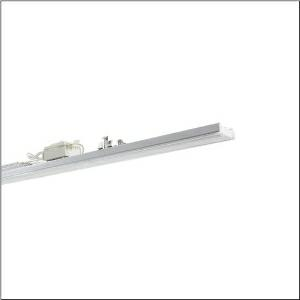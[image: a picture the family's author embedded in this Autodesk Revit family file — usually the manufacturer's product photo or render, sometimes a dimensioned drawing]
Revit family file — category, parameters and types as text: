
# Revit family: licross_r__21_recessed_mo_52tl12dn68xg3s_127a
name_source: partatom
category: Lighting Fixtures
units: mm (PartAtom-declared; Revit-internal decimal feet)

## family parameters
Cut with Voids When Loaded = No
Host = Face
Light Source = No
Part Type = Normal
Room Calculation Point = No
Round Connector Dimension = Use Diameter
Shared = No

## types (1)
- --- (1 x LED, 920 lm, 6.7 W, 6500K)
    Apparent Load = 7 VA
    CIE Flux Codes = 72 92 99 100 100
    Color Rendering = 80
    Color Temperature = 6500K
    Default Elevation = 1800 mm
    Description = Licross® 21 Recessed MO, luminaire insert, of sheet steel, galvanised, coil coated, white, length: 1.500mm, width: 66mm, height: 67mm, LED rated luminous flux: 8.000lm, light colour: 865, control gear: DALI 2 (for two DALI lines), with plug, 6-pole, with phase selection, for trunking rail, 14-core, mains connection: 220..240V, AC, 50/60Hz, rated input power: 46W, for emergency light function, halogen-free wiring, for trunking rail, 14-core, converter,control gear: single battery element, battery: LiFePO4, 9Ah, primary optical cover: cover, of PMMA, light emission: direct distribution, primary light characteristic: symmetric, protection rating (complete): IP40, insulation class (complete): insulation class I (protective earthing), certification: CE, UKCA, protection symbol: D if used in an environment without relevant dust loads with corresponding accessories, impact resistance: IK06, permissible ambient temperature for indoor applications: +5..+35°C, standard: EN 60598-2-22, corresponds to IFS (International Featured Standards) requirements for safety and quality in the food industry, reducing of maximum allowable ambient temperature of 5°C with ceiling mounting, LABS conformity tested according to VDMA 24364:2018-05, packaging unit: 1 piece
    Height = 58 mm
    Lamp = 1 x LED
    Lamp Light Flux = 920 lm
    Lamp Power = 6.7 W
    Lamp count = 1
    Length = 1500 mm
    Luminous efficacy = 137 lm/W
    Manufacturer = Siteco
    ModVariant = No
    Model = 52TL12DN68XG3S
    Mounting Place = Ceiling
    Mounting Type = Pendant
    Number of Poles = 1
    OnlyDefault = Yes
    Power Factor = 1
    Product Name = Licross® 21 Recessed MO
    Product group = luminaire insert
    ProductGroupID = 902
    Protection Class = Protection class I
    Protection Degree = IP 40
    RLX_Detail_Level = 1
    RLX_Emergency_Light_Flux = 0 lm
    RLX_Emergency_Type = 0
    RLX_Emergency_Type_DB = No
    RlxData = <blob elided: 24965 chars, md5=80e0ae62>
    Socket = socket
    Standby Power = 0 W
    System Light Flux = 920 lm
    System Power = 7 W
    Type Comments = : emergency light operation: 3 h
    Type Image = l_1296930.jpg
    URL = http://relux.com
    VarID = @adj_010447
    Voltage = 0 V
    Weight = 0.00 kg
    Width = 66 mm

## geometry (parser evidence)
native form markers: Blend x4, Sweep x12
no freeform markers — native parametric forms only
